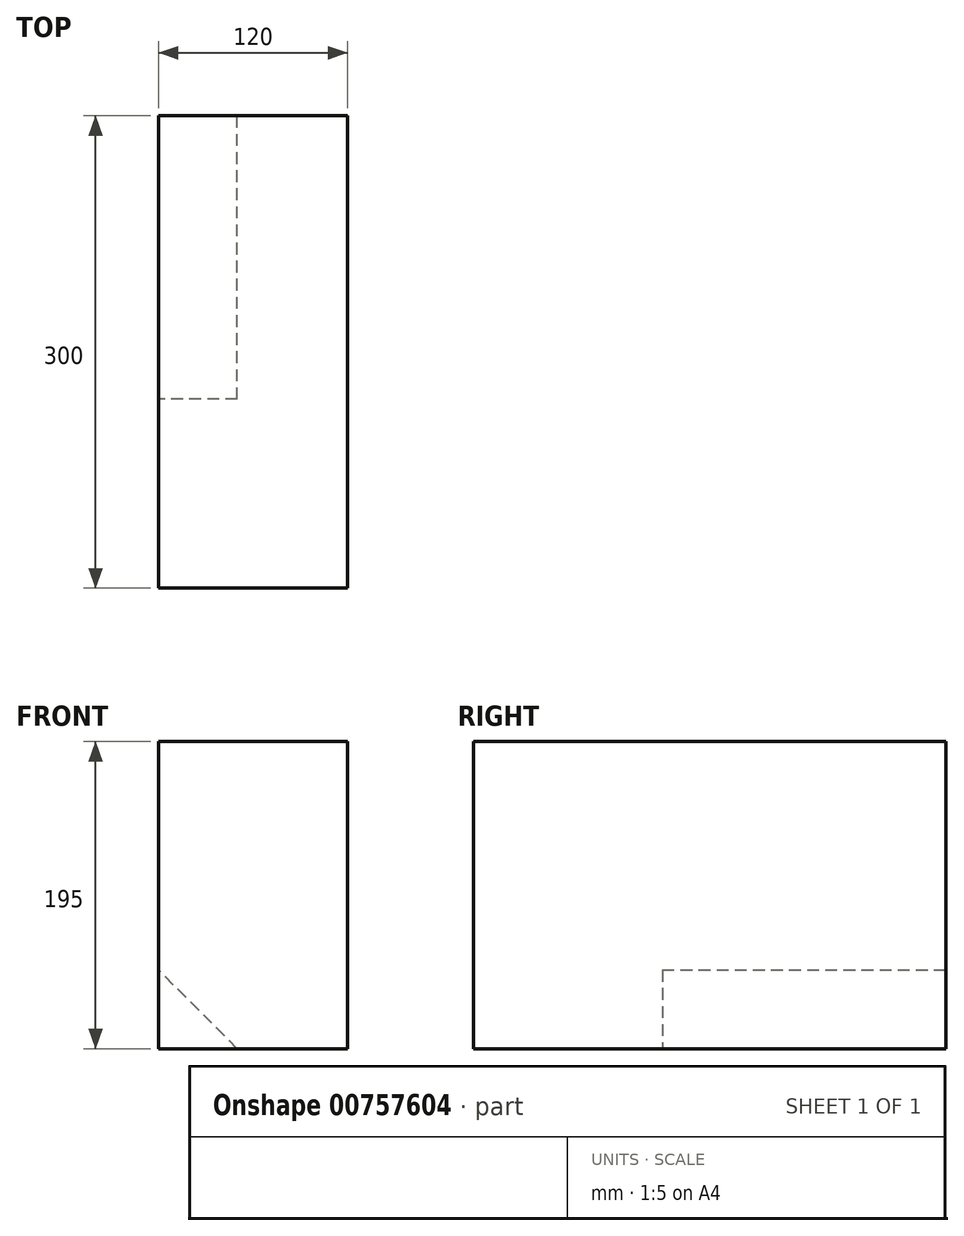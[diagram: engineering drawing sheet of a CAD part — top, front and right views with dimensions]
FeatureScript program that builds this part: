
annotation { "Feature Type Name" : "Feature", "Feature Type Description" : "" }
export const myFeature = defineFeature(function(context is Context, id is Id, definition is map)
    precondition{}
    {
        {
            var Q0;
            Q0=qCreatedBy(makeId("Right.planeOp"),FACE);
            var sketch = newSketch(context, id + "F0", { "sketchPlane" : qUnion([Q0])});
            skLineSegment(sketch, "E0.bottom", {"start": v(130, 0) * mm, "end": v(-170, 0) * mm});
            skLineSegment(sketch, "E0.top", {"start": v(130, -195) * mm, "end": v(-170, -195) * mm});
            skLineSegment(sketch, "E0.left", {"start": v(130, 0) * mm, "end": v(130, -195) * mm});
            skLineSegment(sketch, "E0.right", {"start": v(-170, 0) * mm, "end": v(-170, -195) * mm});
            skSolve(sketch);
        }
        {
            var Q0;
            Q0=makeQuery(id+"F0.imprint","IMPRINT",FACE,{"disambiguationData":[TD([[makeQuery(id+"F0.imprint","IMPRINT",EDGE,{"derivedFrom":sQuery(id+"F0.wireOp",EDGE,"E0.bottom")}),1.0]])]});
            extrude(context, id + "F1", {"entities" : qUnion([Q0]), "endBound" : BoundingType.SYMMETRIC, "depth" : 120 * mm, "offsetDistance" : 25.4 * mm});
        }
        {
            var Q0;
            Q0=makeQuery(id+"F1.opExtrude","SWEPT_FACE",FACE,{"disambiguationData":[OSD([sQuery(id+"F0.wireOp",EDGE,"E0.left")])]});
            var sketch = newSketch(context, id + "F2", { "sketchPlane" : qUnion([Q0])});
            skLineSegment(sketch, "E1", {"start": v(10, -195) * mm, "end": v(60, -145) * mm});
            skLineSegment(sketch, "E2", {"start": v(60, -145) * mm, "end": v(60, -195) * mm});
            skLineSegment(sketch, "E3", {"start": v(60, -195) * mm, "end": v(10, -195) * mm});
            skSolve(sketch);
        }
        {
            var Q0;
            Q0=makeQuery(id+"F2.imprint","IMPRINT",FACE,{"disambiguationData":[TD([[makeQuery(id+"F2.imprint","IMPRINT",EDGE,{"derivedFrom":sQuery(id+"F2.wireOp",EDGE,"E1")}),-1.0]])]});
            extrude(context, id + "F3", {"entities" : qUnion([Q0]), "operationType" : NewBodyOperationType.REMOVE, "oppositeDirection" : true, "depth" : 180 * mm, "offsetDistance" : 25 * mm});
        }
        {
            var Q0;
            Q0=makeQuery(id+"F1.opExtrude","CAP_EDGE",EDGE,{"disambiguationData":[OSD([sQuery(id+"F0.wireOp",EDGE,"E0.top")])],"isStart":true});
            cPoint(context, id + "F4", {"entities" : qUnion([Q0]), "parameter" : 0.5});
        }
        {
            var Q0;
            Q0=makeQuery(id+"F3.boolean.opBoolean","COPY",VERTEX,{"derivedFrom":makeQuery(id+"F3.opExtrude","CAP_VERTEX",VERTEX,{"disambiguationData":[OSD([sQuery(id+"F0.wireOp",EDGE,"E0.top"),sQuery(id+"F0.wireOp",EDGE,"E0.left"),sQuery(id+"F2.wireOp",EDGE,"E1"),sQuery(id+"F2.wireOp",EDGE,"E3")])],"isStart":false})});
            var Q1;
            Q1=makeQuery(id+"F3.boolean.opBoolean","COPY",VERTEX,{"derivedFrom":makeQuery(id+"F3.opExtrude","CAP_VERTEX",VERTEX,{"disambiguationData":[OSD([sQuery(id+"F0.wireOp",EDGE,"E0.left"),sQuery(id+"F2.wireOp",EDGE,"E1"),sQuery(id+"F2.wireOp",EDGE,"E2")])],"isStart":false})});
            var Q2;
            Q2 = qCreatedBy(id + "F4" ,VERTEX);
            cPlane(context, id + "F5", {"entities" : qUnion([Q0, Q1, Q2]), "cplaneType" : CPlaneType.THREE_POINT, "offset" : 25 * mm, "width" : 150 * mm, "height" : 150 * mm});
        }
        {
            var Q0;
            Q0=qCreatedBy(id+"F5.planeOp",FACE);
            var sketch = newSketch(context, id + "F6", { "sketchPlane" : qUnion([Q0])});
            skLineSegment(sketch, "E4", {"start": v(0.78, 131.24) * mm, "end": v(63.83, 163.25) * mm});
            skLineSegment(sketch, "E5", {"start": v(0.78, 209.34) * mm, "end": v(63.83, 163.25) * mm});
            skLineSegment(sketch, "E6", {"start": v(0.78, 209.34) * mm, "end": v(0.78, 131.24) * mm});
            skLineSegment(sketch, "E7", {"start": v(63.83, 163.25) * mm, "end": v(0.78, 209.34) * mm});
            skLineSegment(sketch, "E8", {"start": v(152.1, 98.72) * mm, "end": v(63.83, 163.25) * mm});
            skSolve(sketch);
        }
        {
            var Q0;
            Q0 = qSketchRegion(id + "F6", true);
            extrude(context, id + "F7", {"entities" : qUnion([Q0]), "operationType" : NewBodyOperationType.REMOVE, "endBound" : BoundingType.THROUGH_ALL, "depth" : 25 * mm, "offsetDistance" : 25 * mm});
        }
    });
